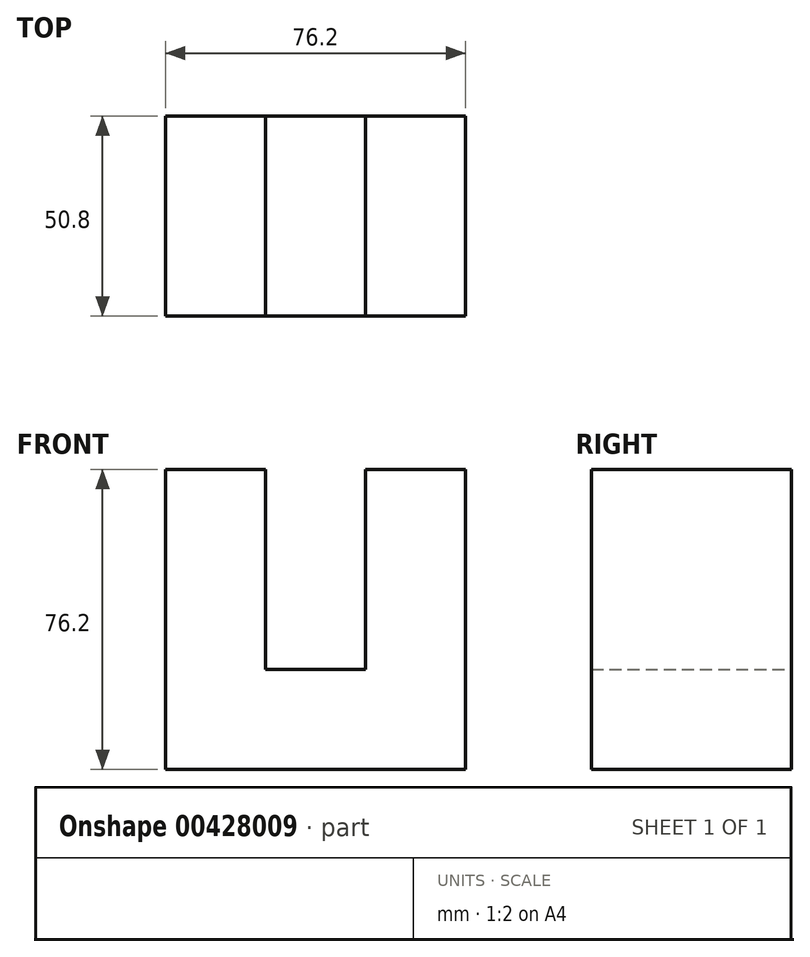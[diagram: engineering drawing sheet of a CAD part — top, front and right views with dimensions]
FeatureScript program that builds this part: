
annotation { "Feature Type Name" : "Feature", "Feature Type Description" : "" }
export const myFeature = defineFeature(function(context is Context, id is Id, definition is map)
    precondition{}
    {
        {
            var Q0;
            Q0=qCreatedBy(makeId("Front.planeOp"),FACE);
            var sketch = newSketch(context, id + "F0", { "sketchPlane" : qUnion([Q0])});
            skLineSegment(sketch, "E0.bottom", {"start": v(0, 0) * mm, "end": v(-76.2, 0) * mm});
            skLineSegment(sketch, "E0.top", {"start": v(0, 76.2) * mm, "end": v(-25.4, 76.2) * mm});
            skLineSegment(sketch, "E0.left", {"start": v(0, 0) * mm, "end": v(0, 76.2) * mm});
            skLineSegment(sketch, "E0.right", {"start": v(-76.2, 0) * mm, "end": v(-76.2, 76.2) * mm});
            skLineSegment(sketch, "E1", {"start": v(-76.2, 76.2) * mm, "end": v(-50.8, 76.2) * mm});
            skLineSegment(sketch, "E2", {"start": v(-50.8, 76.2) * mm, "end": v(-50.8, 25.4) * mm});
            skLineSegment(sketch, "E3", {"start": v(-50.8, 25.4) * mm, "end": v(-25.4, 25.4) * mm});
            skLineSegment(sketch, "E4", {"start": v(-25.4, 25.4) * mm, "end": v(-25.4, 76.2) * mm});
            skLineSegment(sketch, "E5", {"start": v(-25.4, 76.2) * mm, "end": v(0, 76.2) * mm});
            skLineSegment(sketch, "E6.trimOffspring", {"start": v(-50.8, 76.2) * mm, "end": v(-76.2, 76.2) * mm});
            skSolve(sketch);
        }
        {
            var Q0;
            Q0 = qSketchRegion(id + "F0", true);
            extrude(context, id + "F1", {"entities" : qUnion([Q0]), "depth" : 50.8 * mm});
        }
    });
